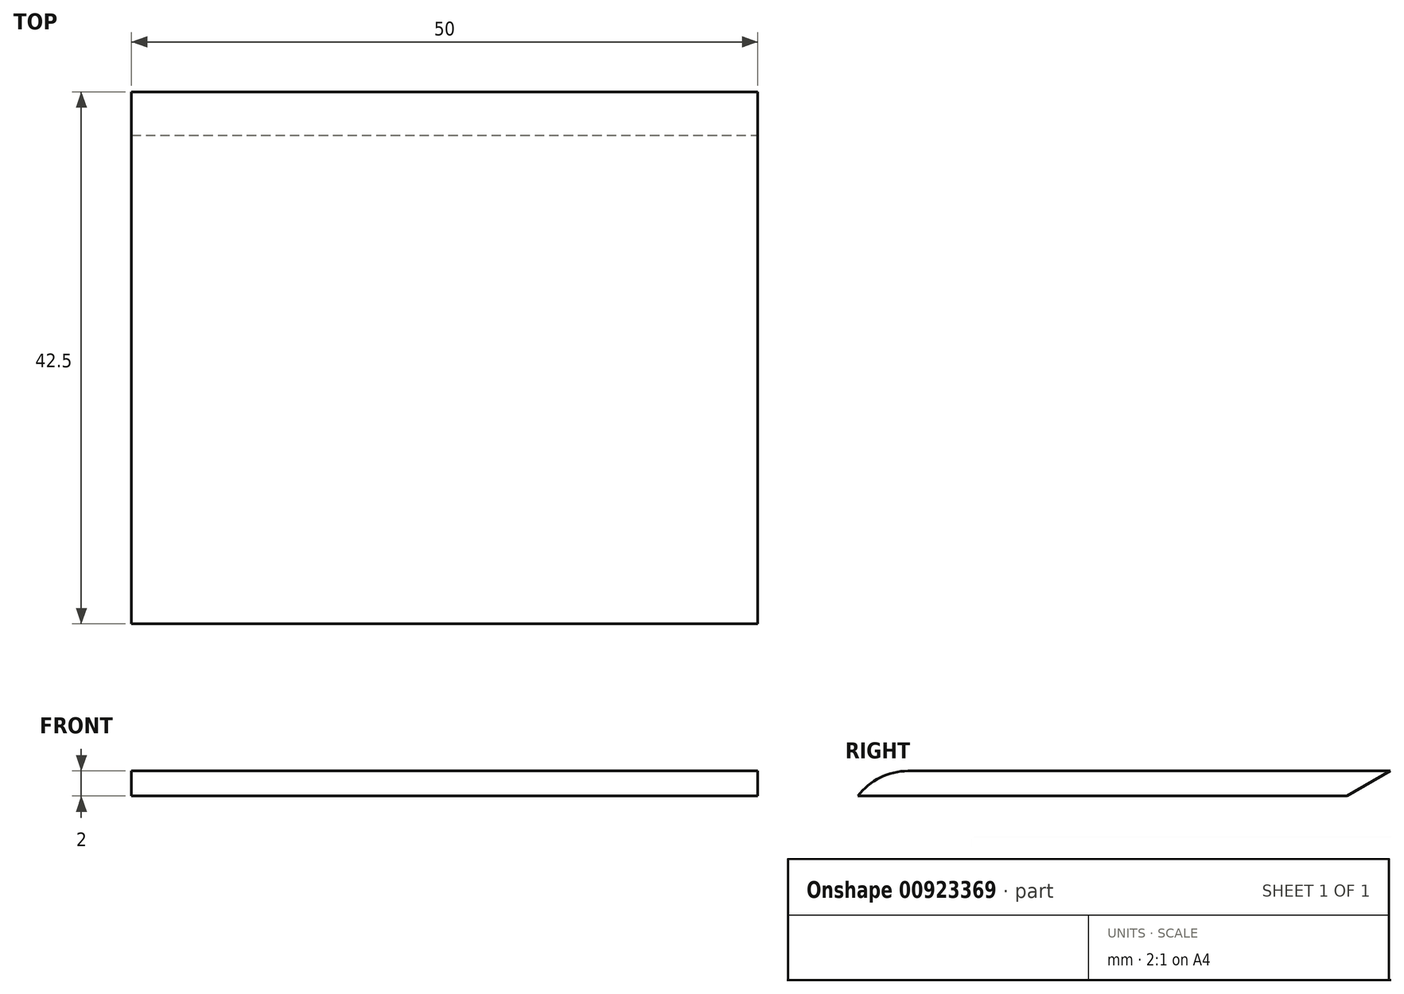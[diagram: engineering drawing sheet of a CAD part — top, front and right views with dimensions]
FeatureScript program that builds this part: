
annotation { "Feature Type Name" : "Feature", "Feature Type Description" : "" }
export const myFeature = defineFeature(function(context is Context, id is Id, definition is map)
    precondition{}
    {
        {
            var Q0;
            Q0=qCreatedBy(makeId("Top.planeOp"),FACE);
            var sketch = newSketch(context, id + "F0", { "sketchPlane" : qUnion([Q0])});
            skLineSegment(sketch, "E0.bottom", {"start": v(0, 0) * mm, "end": v(-50, 0) * mm});
            skLineSegment(sketch, "E0.top", {"start": v(0, -42.5) * mm, "end": v(-50, -42.5) * mm});
            skLineSegment(sketch, "E0.left", {"start": v(0, 0) * mm, "end": v(0, -42.5) * mm});
            skLineSegment(sketch, "E0.right", {"start": v(-50, 0) * mm, "end": v(-50, -42.5) * mm});
            skSolve(sketch);
        }
        {
            var Q0;
            Q0=makeQuery(id+"F0.imprint","IMPRINT",FACE,{"disambiguationData":[TD([[makeQuery(id+"F0.imprint","IMPRINT",EDGE,{"derivedFrom":sQuery(id+"F0.wireOp",EDGE,"E0.bottom")}),1.0]])]});
            extrude(context, id + "F1", {"entities" : qUnion([Q0]), "depth" : 2 * mm, "offsetDistance" : 25 * mm});
        }
        {
            var Q0;
            Q0=makeQuery(id+"F1.opExtrude","CAP_EDGE",EDGE,{"disambiguationData":[OSD([sQuery(id+"F0.wireOp",EDGE,"E0.bottom")])],"isStart":true});
            chamfer(context, id + "F2", {"entities" : qUnion([Q0]), "chamferType" : ChamferType.OFFSET_ANGLE, "width" : 2 * mm, "oppositeDirection" : false, "angle" : 60 * degree, "tangentPropagation" : true});
        }
        {
            var Q0;
            Q0=makeQuery(id+"F1.opExtrude","CAP_EDGE",EDGE,{"disambiguationData":[OSD([sQuery(id+"F0.wireOp",EDGE,"E0.top")])],"isStart":false});
            fillet(context, id + "F3", {"entities" : qUnion([Q0]), "radius" : 5 * mm, "tangentPropagation" : true, "allowEdgeOverflow" : false});
        }
    });
